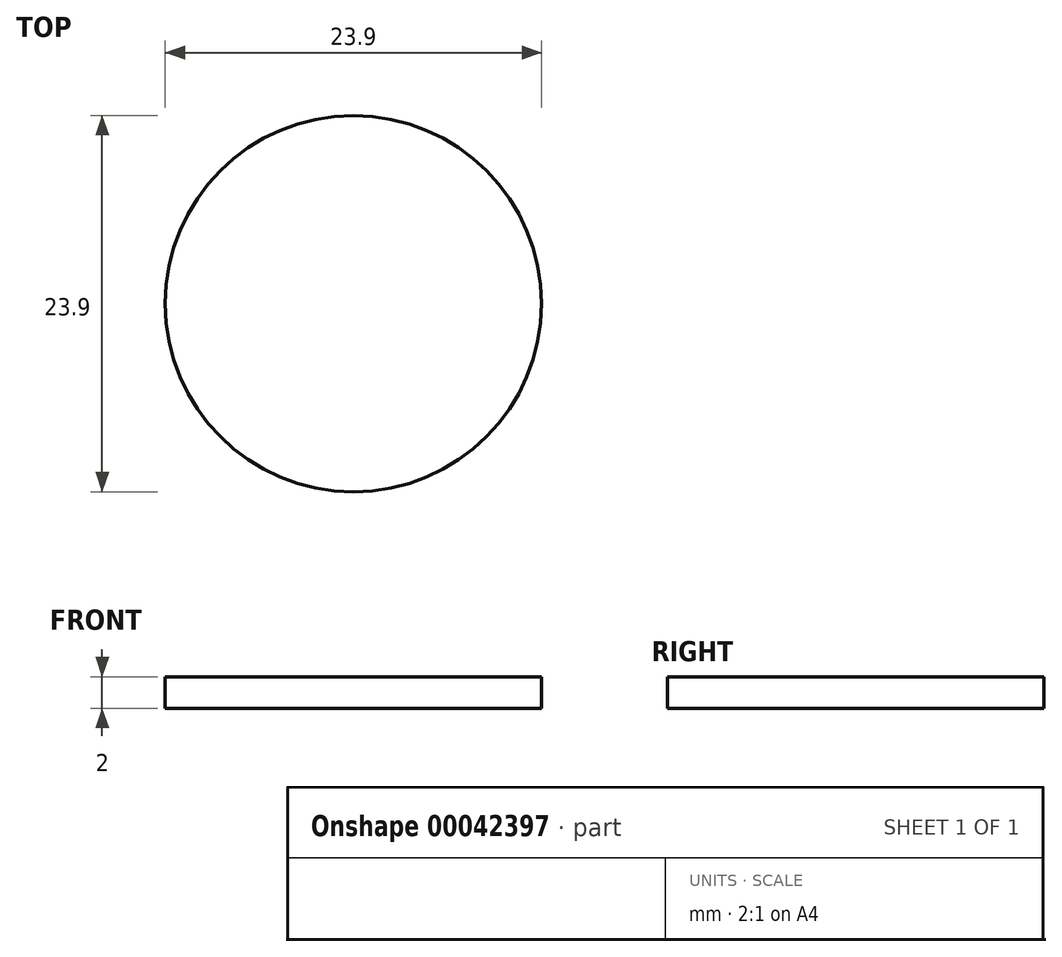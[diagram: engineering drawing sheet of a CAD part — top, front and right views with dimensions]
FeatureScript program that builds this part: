
annotation { "Feature Type Name" : "Feature", "Feature Type Description" : "" }
export const myFeature = defineFeature(function(context is Context, id is Id, definition is map)
    precondition{}
    {
        {
            var Q0;
            Q0=qCreatedBy(makeId("Top.planeOp"),FACE);
            var sketch = newSketch(context, id + "F0", { "sketchPlane" : qUnion([Q0])});
            skCircle(sketch, "E0", {"center": v(0, 0) * mm, "radius": 11.95 * mm});
            skSolve(sketch);
        }
        {
            var Q0;
            Q0=makeQuery(id+"F0.imprint","IMPRINT",FACE,{"disambiguationData":[TD([[makeQuery(id+"F0.imprint","IMPRINT",EDGE,{"derivedFrom":sQuery(id+"F0.wireOp",EDGE,"E0")}),1.0]])]});
            extrude(context, id + "F1", {"entities" : qUnion([Q0]), "depth" : 2 * mm});
        }
    });
